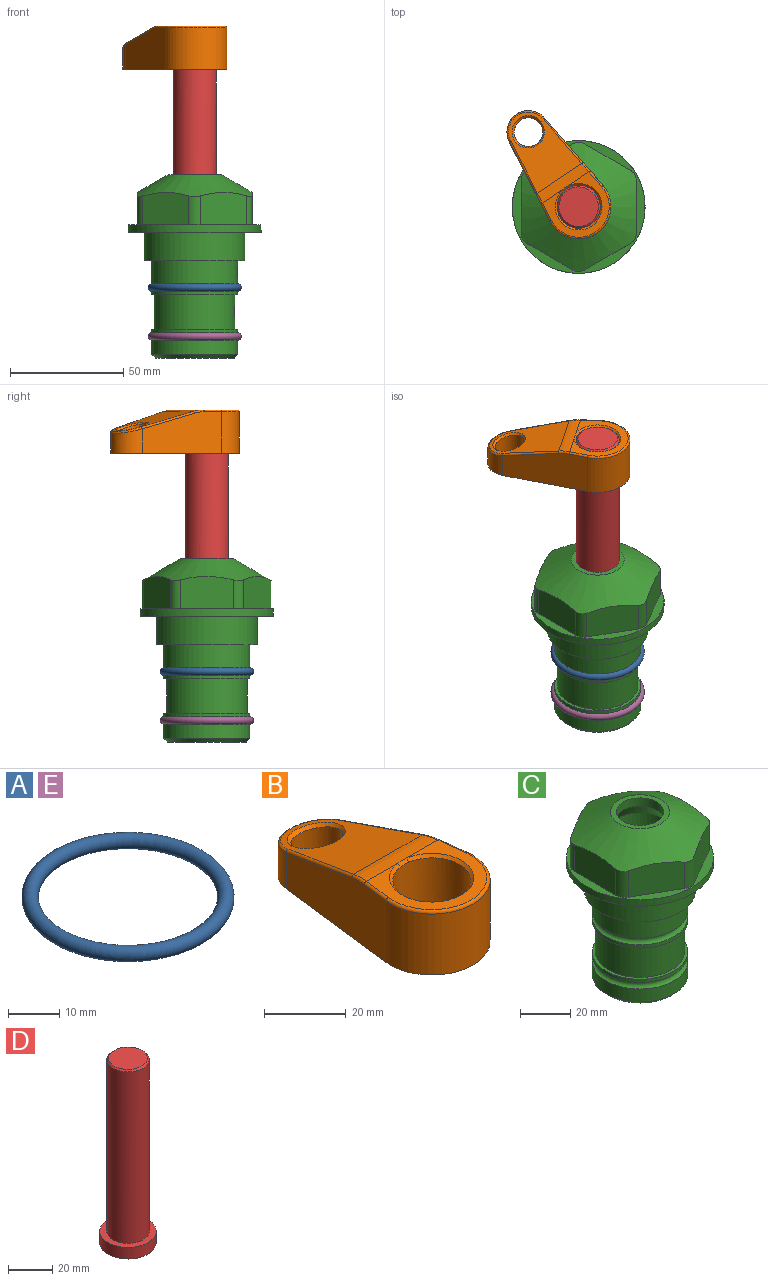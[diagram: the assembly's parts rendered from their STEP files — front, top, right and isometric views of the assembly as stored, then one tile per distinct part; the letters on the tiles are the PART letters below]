
ASSEMBLY  parts=5 mates=4
PART A: 1 faces, bbox 44.7x44.7x3.2 mm
  f0: torus R=19.05mm, axis (0,0,1), area 1193.9mm2
PART B: 31 faces, bbox 31.7x65.5x19.8 mm
  f0: plane 39.12x18.26mm, normal (0.99,0.12,0), area 612.2mm2, adj f1,f4,f7,f11,f13,f15
  f1: cylinder r=9.53mm len=18.91mm, axis (0,0,-1), area 296.1mm2, adj f0,f2,f7,f17
  f2: plane 39.12x18.26mm, normal (-0.99,0.12,0), area 612.2mm2, adj f1,f4,f7,f12,f14,f16
  f3: cylinder r=6.35mm len=12.7mm, axis (0,0,-1), area 362.4mm2, adj f7,f18
  f4: cylinder r=14.29mm len=28.58mm, axis (0,0,-1), area 882.2mm2, adj f0,f2,f7,f10
  f5: cylinder r=9.53mm len=19.05mm, axis (0,0,-1), area 1092.6mm2, adj f7,f19,f20
  f6: plane 26.99x23.69mm, normal (0,0,1), area 216.2mm2, adj f9,f10,f11,f12,f19
  f7: plane 63.5x28.58mm, normal (0,0,-1), area 661.8mm2, adj f0,f1,f2,f3,f4,f5,f22,f23
  f8: plane 33.52x23.6mm, normal (0,0.26,0.97), area 486mm2, adj f9,f15,f16,f17,f18
  f9: cylinder r=19.05mm len=24.72mm, axis (1,0,0), area 120.4mm2, adj f6,f8,f13,f14,f20
  f10: torus R=13.49mm, axis (0,0,1), area 59mm2, adj f4,f6,f11,f12
  f11: cylinder r=0.79mm len=8.67mm, axis (0.12,-0.99,0), area 10.8mm2, adj f0,f6,f10,f13
  f12: cylinder r=0.79mm len=8.67mm, axis (0.12,0.99,0), area 10.8mm2, adj f2,f6,f10,f14
  f13: bspline ~4.95x1.42mm, area 6.1mm2, adj f0,f9,f11,f15
  f14: bspline ~4.95x1.42mm, area 6.1mm2, adj f2,f9,f12,f16
  f15: cylinder r=0.79mm len=25.95mm, axis (0.12,-0.96,0.26), area 32.9mm2, adj f0,f8,f13,f17
  f16: cylinder r=0.79mm len=25.95mm, axis (0.12,0.96,-0.26), area 32.9mm2, adj f2,f8,f14,f17
  f17: bspline ~18.91x8.38mm, area 30mm2, adj f1,f8,f15,f16
  f18: bspline ~14.29x14.29mm, area 48.3mm2, adj f3,f8
  f19: cone r=9.53mm half-angle=45deg, axis (0,0,1), area 66.5mm2, adj f5,f6,f20
  f20: bspline ~3.22x0.96mm, area 3.5mm2, adj f5,f9,f19
  f21: plane 2.75x2.72mm, normal (0,0,-1), area 2.9mm2, adj f23,f25,f28
  f22: plane 23.05x15.88mm, normal (-0.99,-0.12,0), area 323.6mm2, adj f7,f25,f26,f27,f28,f29
  f23: plane 23.05x15.88mm, normal (0.99,-0.12,0), area 323.6mm2, adj f7,f21,f25,f27,f28,f30
  f24: cylinder r=9.53mm len=10.69mm, axis (0,0,-1), area 114.7mm2, adj f7,f27,f29,f30
  f25: cylinder r=12.7mm len=20.59mm, axis (0,0,-1), area 381.1mm2, adj f7,f21,f22,f23,f26,f28
  f26: plane 2.75x2.72mm, normal (0,0,-1), area 2.9mm2, adj f22,f25,f28
  f27: plane 19.72x18.37mm, normal (0,-0.26,-0.97), area 291.8mm2, adj f22,f23,f24,f28,f29,f30
  f28: cylinder r=15.88mm len=19.92mm, axis (1,0,0), area 54.8mm2, adj f21,f22,f23,f25,f26,f27
  f29: cylinder r=1.59mm len=11mm, axis (0,0,-1), area 34.7mm2, adj f7,f22,f24,f27
  f30: cylinder r=1.59mm len=11mm, axis (0,0,-1), area 34.7mm2, adj f7,f23,f24,f27
PART C: 36 faces, bbox 58.7x58.7x81 mm
  f0: cylinder r=17.78mm len=35.56mm, axis (0,0,1), area 1670.8mm2, adj f23,f24,f31
  f1: cylinder r=19.05mm len=38.1mm, axis (0,0,1), area 1191.9mm2, adj f26,f27,f30
  f2: plane 58.66x58.66mm, normal (0,0,-1), area 1150.6mm2, adj f3,f28
  f3: cylinder r=29.33mm len=58.66mm, axis (0,0,-1), area 585.1mm2, adj f2,f4
  f4: plane 58.66x58.66mm, normal (0,0,1), area 475.9mm2, adj f3,f5,f6,f7,f8,f9,f10,f11
  f5: plane 20.32x14.34mm, normal (-0.5,0.87,0), area 324.4mm2, adj f4,f15,f16,f17
  f6: plane 20.32x14.34mm, normal (0.5,0.87,0), area 324.4mm2, adj f4,f14,f15,f17
  f7: plane 23.48x14.34mm, normal (1,0,0), area 324.4mm2, adj f4,f13,f14,f17
  f8: plane 20.32x14.34mm, normal (0.5,-0.87,0), area 324.4mm2, adj f4,f12,f13,f17
  f9: plane 20.32x14.34mm, normal (-0.5,-0.87,0), area 324.4mm2, adj f4,f11,f12,f17
  f10: plane 23.48x14.34mm, normal (-1,0,0), area 324.4mm2, adj f4,f11,f16,f17
  f11: cylinder r=5.08mm len=12.85mm, axis (0,0,-1), area 67.2mm2, adj f4,f9,f10,f17
  f12: cylinder r=5.08mm len=12.85mm, axis (0,0,-1), area 67.2mm2, adj f4,f8,f9,f17
  f13: cylinder r=5.08mm len=12.85mm, axis (0,0,-1), area 67.2mm2, adj f4,f7,f8,f17
  f14: cylinder r=5.08mm len=12.85mm, axis (0,0,-1), area 67.2mm2, adj f4,f6,f7,f17
  f15: cylinder r=5.08mm len=12.85mm, axis (0,0,-1), area 67.2mm2, adj f4,f5,f6,f17
  f16: cylinder r=5.08mm len=12.85mm, axis (0,0,-1), area 67.2mm2, adj f4,f5,f10,f17
  f17: cone r=11.73mm half-angle=60deg, axis (0,0,-1), area 2071.8mm2, adj f5,f6,f7,f8,f9,f10,f11,f12
  f18: plane 23.46x23.46mm, normal (0,0,1), area 147.4mm2, adj f17,f35
  f19: plane 34.93x34.93mm, normal (0,0,-1), area 958mm2, adj f29
  f20: cylinder r=19.05mm len=38.1mm, axis (0,0,1), area 760.1mm2, adj f21,f29
  f21: torus R=19.05mm, axis (0,0,1), area 565.3mm2, adj f20,f22
  f22: cylinder r=19.05mm len=38.1mm, axis (0,0,1), area 190mm2, adj f21,f23
  f23: plane 38.1x38.1mm, normal (0,0,1), area 146.9mm2, adj f0,f22
  f24: plane 38.1x38.1mm, normal (0,0,-1), area 146.9mm2, adj f0,f25
  f25: cylinder r=19.05mm len=38.1mm, axis (0,0,1), area 190mm2, adj f24,f26
  f26: torus R=19.05mm, axis (0,0,1), area 565.3mm2, adj f1,f25
  f27: plane 44.45x44.45mm, normal (0,0,-1), area 411.7mm2, adj f1,f28
  f28: cylinder r=22.23mm len=44.45mm, axis (0,0,1), area 1773.5mm2, adj f2,f27
  f29: cone r=19.05mm half-angle=45deg, axis (0,0,1), area 257.5mm2, adj f19,f20
  f30: cylinder r=3.17mm len=6.75mm, axis (-1,0,0), area 128mm2, adj f1,f33
  f31: cylinder r=3.17mm len=6.35mm, axis (-1,0,0), area 102.5mm2, adj f0,f33
  f32: plane 25.4x25.4mm, normal (0,0,1), area 506.7mm2, adj f33
  f33: cylinder r=12.7mm len=66.42mm, axis (0,0,-1), area 5236.2mm2, adj f30,f31,f32,f34
  f34: cone r=9.53mm half-angle=30deg, axis (0,0,-1), area 443.4mm2, adj f33,f35
  f35: cylinder r=9.53mm len=19.05mm, axis (0,0,-1), area 240.9mm2, adj f18,f34
PART D: 6 faces, bbox 25.4x25.4x101.6 mm
  f0: plane 17.46x17.46mm, normal (0,0,1), area 239.5mm2, adj f5
  f1: plane 25.4x25.4mm, normal (0,0,-1), area 506.7mm2, adj f2
  f2: cylinder r=12.7mm len=25.4mm, axis (0,0,1), area 506.7mm2, adj f1,f3
  f3: plane 25.4x25.4mm, normal (0,0,1), area 221.7mm2, adj f2,f4
  f4: cylinder r=9.53mm len=94.46mm, axis (0,0,1), area 5653mm2, adj f3,f5
  f5: cone r=8.73mm half-angle=45deg, axis (0,0,-1), area 64.4mm2, adj f0,f4
PART E: same geometry as A
PLACE A at identity
PLACE B rot(axis=(0,0,1),33.9deg) t=(0,0,27.55)mm
PLACE C at identity fixed
PLACE D rot(axis=(0,0,1),33.9deg) t=(0,0,27.55)mm
PLACE E t=(0,0,-21.59)mm
MATE fastened D.f2 <-> B.f4  axis (0,0,1) through (0,0,90.26)mm
MATE fastened A.f0 <-> C.f0  axis (0,0,1) through (0,0,-24.51)mm
MATE cylindrical D.f2 <-> C.f0  axis (0,0,-1) through (0,0,-10.55)mm
MATE fastened E.f0 <-> C.f0  axis (0,0,1) through (0,0,-46.1)mm
